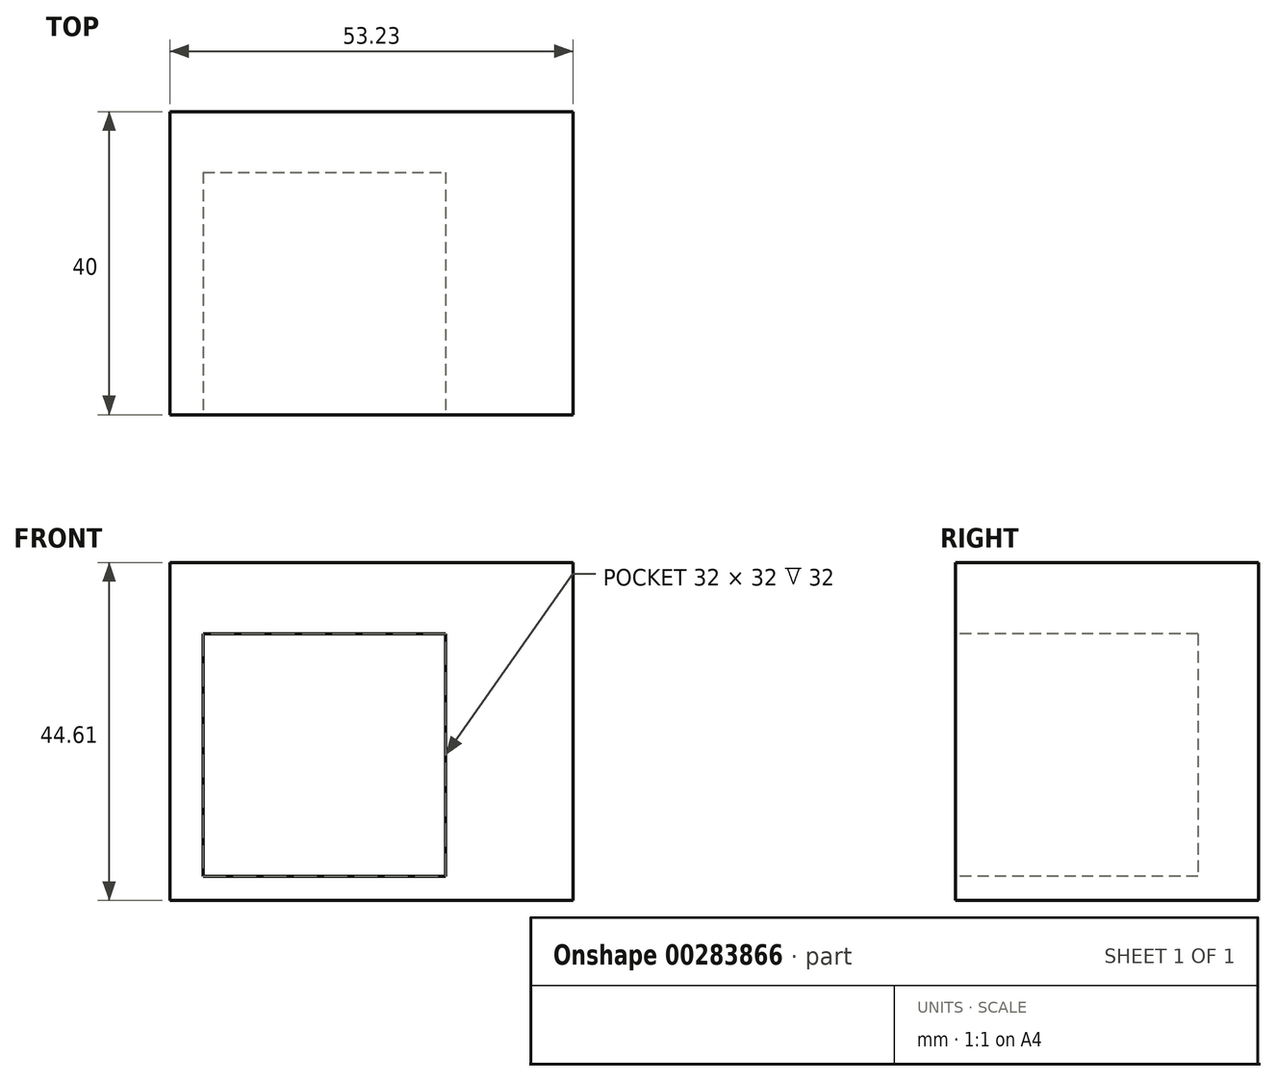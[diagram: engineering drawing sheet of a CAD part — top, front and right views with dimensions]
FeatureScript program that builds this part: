
annotation { "Feature Type Name" : "Feature", "Feature Type Description" : "" }
export const myFeature = defineFeature(function(context is Context, id is Id, definition is map)
    precondition{}
    {
        {
            var Q0;
            Q0=qCreatedBy(makeId("Front.planeOp"),FACE);
            var sketch = newSketch(context, id + "F0", { "sketchPlane" : qUnion([Q0])});
            skLineSegment(sketch, "E0", {"start": v(0, 0) * mm, "end": v(0, 44.61) * mm});
            skLineSegment(sketch, "E1", {"start": v(0, 44.61) * mm, "end": v(53.23, 44.61) * mm});
            skLineSegment(sketch, "E2", {"start": v(53.23, 44.61) * mm, "end": v(53.23, 0) * mm});
            skLineSegment(sketch, "E3", {"start": v(53.23, 0) * mm, "end": v(0, 0) * mm});
            skSolve(sketch);
        }
        {
            var Q0;
            Q0=makeQuery(id+"F0.imprint","IMPRINT",FACE,{"disambiguationData":[TD([[makeQuery(id+"F0.imprint","IMPRINT",EDGE,{"derivedFrom":sQuery(id+"F0.wireOp",EDGE,"E0")}),-1.0]])]});
            extrude(context, id + "F1", {"entities" : qUnion([Q0]), "depth" : 40 * mm});
        }
        {
            var Q0;
            Q0=makeQuery(id+"F1.opExtrude","CAP_FACE",FACE,{"disambiguationData":[OSD([sQuery(id+"F0.wireOp",EDGE,"E0"),sQuery(id+"F0.wireOp",EDGE,"E1"),sQuery(id+"F0.wireOp",EDGE,"E2"),sQuery(id+"F0.wireOp",EDGE,"E3")])],"isStart":false});
            var sketch = newSketch(context, id + "F2", { "sketchPlane" : qUnion([Q0])});
            skLineSegment(sketch, "E4.bottom", {"start": v(4.42, 35.18) * mm, "end": v(36.42, 35.18) * mm});
            skLineSegment(sketch, "E4.top", {"start": v(4.42, 3.18) * mm, "end": v(36.42, 3.18) * mm});
            skLineSegment(sketch, "E4.left", {"start": v(4.42, 35.18) * mm, "end": v(4.42, 3.18) * mm});
            skLineSegment(sketch, "E4.right", {"start": v(36.42, 35.18) * mm, "end": v(36.42, 3.18) * mm});
            skSolve(sketch);
        }
        {
            var Q0;
            Q0 = qSketchRegion(id + "F2", true);
            extrude(context, id + "F3", {"entities" : qUnion([Q0]), "operationType" : NewBodyOperationType.REMOVE, "oppositeDirection" : true, "offsetDistance" : 25 * mm, "depth" : 32 * mm});
        }
    });
